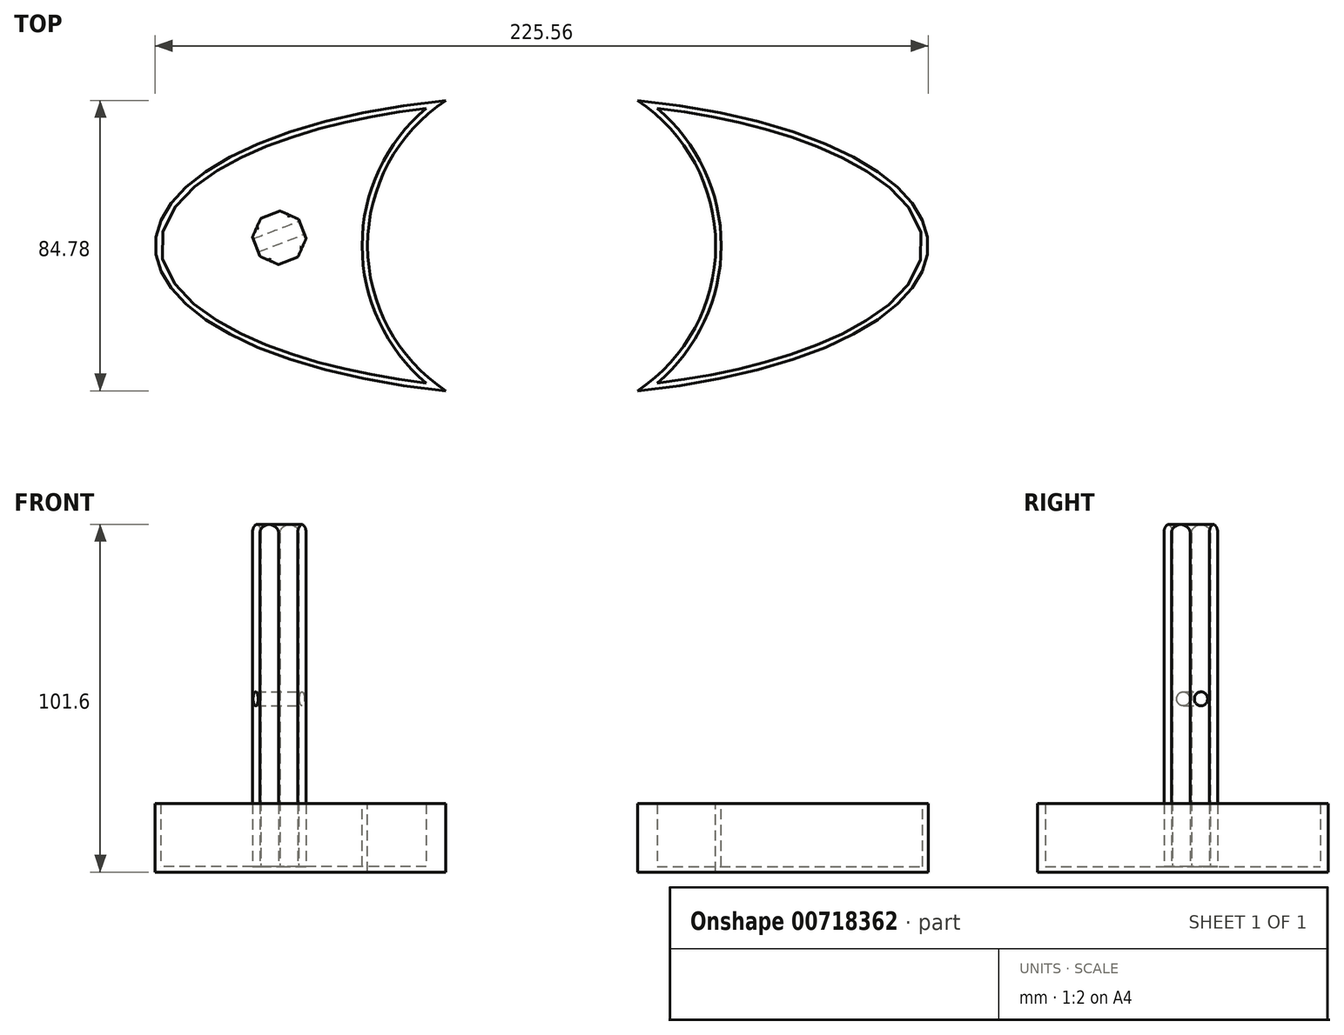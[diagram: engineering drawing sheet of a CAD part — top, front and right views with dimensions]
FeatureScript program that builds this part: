
annotation { "Feature Type Name" : "Feature", "Feature Type Description" : "" }
export const myFeature = defineFeature(function(context is Context, id is Id, definition is map)
    precondition{}
    {
        {
            var Q0;
            Q0=qCreatedBy(makeId("Top.planeOp"),FACE);
            var sketch = newSketch(context, id + "F0", { "sketchPlane" : qUnion([Q0])});
            skEllipse(sketch, "E0", {"center": v(0, 0) * mm, "majorRadius": 43.76 * mm, "minorRadius": 112.78 * mm, "majorAxis": v(0, 1)});
            skSolve(sketch);
        }
        {
            var Q0;
            Q0 = qSketchRegion(id + "F0", true);
            extrude(context, id + "F1", {"entities" : qUnion([Q0]), "depth" : 20 * mm, "offsetDistance" : 25.4 * mm});
        }
        {
            var Q0;
            Q0=makeQuery(id+"F1.opExtrude","CAP_FACE",FACE,{"disambiguationData":[OSD([sQuery(id+"F0.wireOp",EDGE,"E0")])],"isStart":false});
            var sketch = newSketch(context, id + "F2", { "sketchPlane" : qUnion([Q0])});
            skCircle(sketch, "E1", {"center": v(0, 0) * mm, "radius": 50.8 * mm});
            skSolve(sketch);
        }
        {
            var Q0;
            Q0 = qSketchRegion(id + "F2", true);
            extrude(context, id + "F3", {"entities" : qUnion([Q0]), "operationType" : NewBodyOperationType.REMOVE, "oppositeDirection" : true, "depth" : 25.4 * mm, "offsetDistance" : 25.4 * mm});
        }
        {
            var Q0;
            Q0=makeQuery(id+"F3.boolean.opBoolean","SPLIT",FACE,{"disambiguationData":[OD(0.0)],"derivedFrom":makeQuery(id+"F1.opExtrude","CAP_FACE",FACE,{"disambiguationData":[OSD([sQuery(id+"F0.wireOp",EDGE,"E0")])],"isStart":false})});
            var Q1;
            Q1=makeQuery(id+"F3.boolean.opBoolean","SPLIT",FACE,{"disambiguationData":[OD(1.0)],"derivedFrom":makeQuery(id+"F1.opExtrude","CAP_FACE",FACE,{"disambiguationData":[OSD([sQuery(id+"F0.wireOp",EDGE,"E0")])],"isStart":false})});
            shell(context, id + "F4", {"entities" : qUnion([Q0, Q1]), "thickness" : 1.6 * mm});
        }
        {
            var Q0;
            {var subQ0=sQuery(id+"F0.wireOp",EDGE,"E0");Q0=makeQuery(id+"F4.opShell","OFFSET_FACE",FACE,{"disambiguationData":[OSD([subQ0]),TDD([makeQuery(id+"F3.boolean.opBoolean","SPLIT",FACE,{"disambiguationData":[OD(0.0)],"derivedFrom":makeQuery(id+"F1.opExtrude","CAP_FACE",FACE,{"disambiguationData":[OSD([subQ0])],"isStart":true})})])]});}
            var sketch = newSketch(context, id + "F5", { "sketchPlane" : qUnion([Q0])});
            skCircle(sketch, "E2.cCircle", {"center": v(-76.58, 2.3) * mm, "radius": 7.24 * mm, "construction": true});
            skLineSegment(sketch, "E2.0", {"start": v(-71.18, -3.39) * mm, "end": v(-76.79, -5.53) * mm});
            skLineSegment(sketch, "E2.1", {"start": v(-76.79, -5.53) * mm, "end": v(-82.27, -3.09) * mm});
            skLineSegment(sketch, "E2.2", {"start": v(-82.27, -3.09) * mm, "end": v(-84.41, 2.51) * mm});
            skLineSegment(sketch, "E2.3", {"start": v(-84.41, 2.51) * mm, "end": v(-81.97, 8) * mm});
            skLineSegment(sketch, "E2.4", {"start": v(-81.97, 8) * mm, "end": v(-76.37, 10.14) * mm});
            skLineSegment(sketch, "E2.5", {"start": v(-76.37, 10.14) * mm, "end": v(-70.89, 7.7) * mm});
            skLineSegment(sketch, "E2.6", {"start": v(-70.89, 7.7) * mm, "end": v(-68.74, 2.1) * mm});
            skLineSegment(sketch, "E2.7", {"start": v(-68.74, 2.1) * mm, "end": v(-71.18, -3.39) * mm});
            skPoint(sketch, "E2.0.midPoint", {"position": v(-73.98, -4.46) * mm});
            skSolve(sketch);
        }
        {
            var Q0;
            Q0 = qSketchRegion(id + "F5", true);
            extrude(context, id + "F6", {"entities" : qUnion([Q0]), "operationType" : NewBodyOperationType.ADD, "depth" : 100 * mm, "offsetDistance" : 25.4 * mm});
        }
        {
            var Q0;
            Q0=makeQuery(id+"F6.opExtrude","SWEPT_FACE",FACE,{"disambiguationData":[OSD([sQuery(id+"F5.wireOp",EDGE,"E2.6")])]});
            var sketch = newSketch(context, id + "F7", { "sketchPlane" : qUnion([Q0])});
            skCircle(sketch, "E3", {"center": v(29.95, 50.6) * mm, "radius": 2.05 * mm});
            skSolve(sketch);
        }
        {
            var Q0;
            Q0 = qSketchRegion(id + "F7", true);
            extrude(context, id + "F8", {"entities" : qUnion([Q0]), "operationType" : NewBodyOperationType.REMOVE, "oppositeDirection" : true, "depth" : 25.4 * mm, "offsetDistance" : 25.4 * mm});
        }
        {
            var Q0;
            Q0=makeQuery(id+"F6.opExtrude","SWEPT_FACE",FACE,{"disambiguationData":[OSD([sQuery(id+"F5.wireOp",EDGE,"E2.6")])]});
            var sketch = newSketch(context, id + "F9", { "sketchPlane" : qUnion([Q0])});
            skPoint(sketch, "E4", {"position": v(29.44, 76.75) * mm});
            skSolve(sketch);
        }
        {
            var Q0;
            Q0=sQuery(id+"F9.wireOp",VERTEX,"E4");
            var Q1;
            Q1=makeQuery(id+"F3.boolean.opBoolean","SPLIT",BODY,{"disambiguationData":[OD(0.0)],"derivedFrom":makeQuery(id+"F1.opExtrude","SWEPT_BODY",BODY,{"disambiguationData":[OSD([sQuery(id+"F0.wireOp",EDGE,"E0")])]})});
            hole(context, id + "F10", {"style" : HoleStyle.SIMPLE, "endStyle" : HoleEndStyle.THROUGH, "holeDiameter" : 6.35 * mm, "majorDiameter" : 6.35 * mm, "isTappedThrough" : true, "tappedDepth" : 12.7 * mm, "tapClearance" : 3, "locations" : qUnion([Q0]), "scope" : qUnion([Q1])});
        }
        {
            var Q0;
            Q0=makeQuery(id+"F6.opExtrude","CAP_EDGE",EDGE,{"disambiguationData":[OSD([sQuery(id+"F5.wireOp",EDGE,"E2.0")])],"isStart":false});
            var Q1;
            Q1=makeQuery(id+"F6.opExtrude","CAP_EDGE",EDGE,{"disambiguationData":[OSD([sQuery(id+"F5.wireOp",EDGE,"E2.4")])],"isStart":false});
            var Q2;
            Q2=makeQuery(id+"F6.opExtrude","CAP_EDGE",EDGE,{"disambiguationData":[OSD([sQuery(id+"F5.wireOp",EDGE,"E2.6")])],"isStart":false});
            var Q3;
            Q3=makeQuery(id+"F6.opExtrude","CAP_EDGE",EDGE,{"disambiguationData":[OSD([sQuery(id+"F5.wireOp",EDGE,"E2.2")])],"isStart":false});
            fillet(context, id + "F11", {"entities" : qUnion([Q0, Q1, Q2, Q3]), "radius" : 2.54 * mm, "tangentPropagation" : true, "allowEdgeOverflow" : false});
        }
    });
